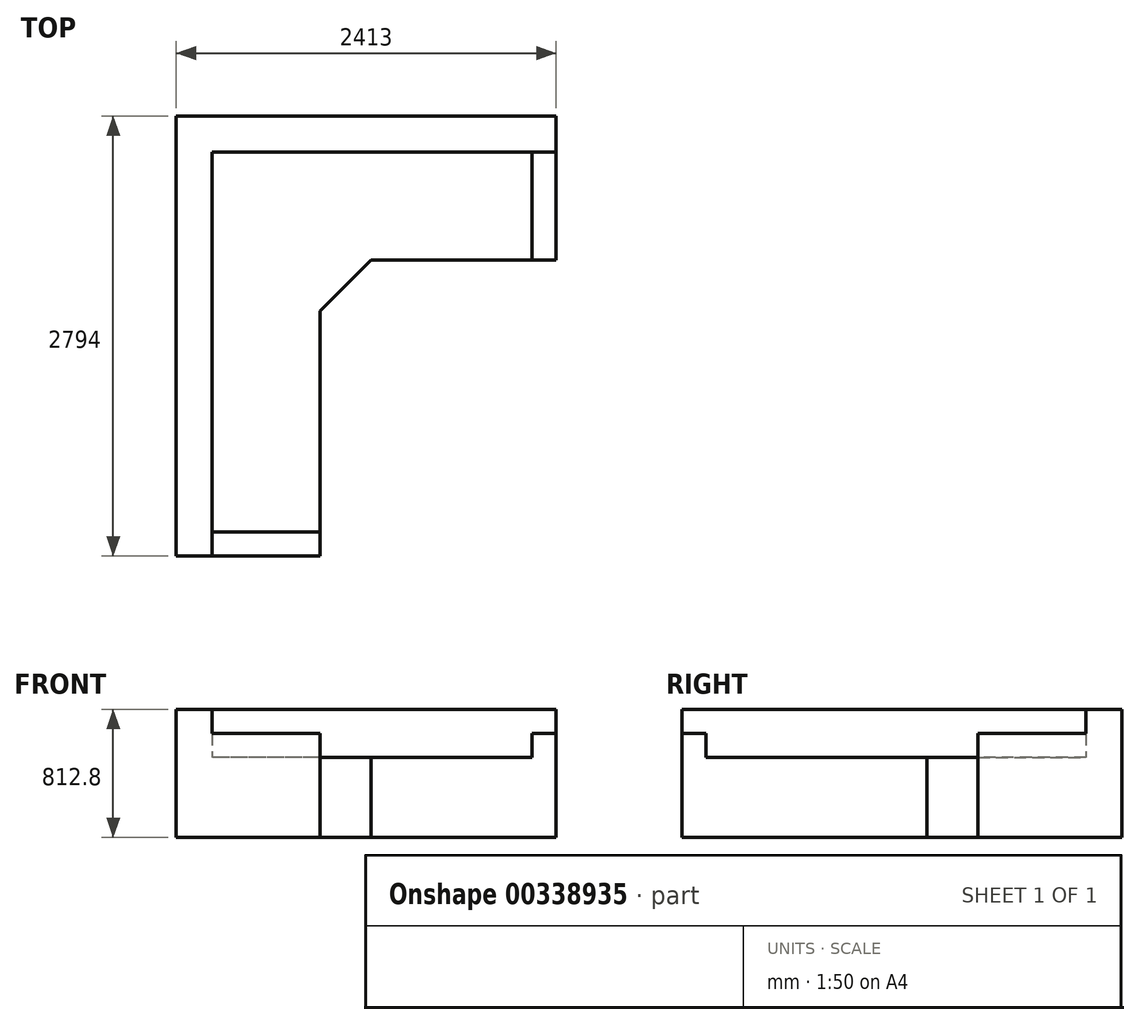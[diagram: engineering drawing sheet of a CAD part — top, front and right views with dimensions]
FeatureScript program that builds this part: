
annotation { "Feature Type Name" : "Feature", "Feature Type Description" : "" }
export const myFeature = defineFeature(function(context is Context, id is Id, definition is map)
    precondition{}
    {
        {
            var Q0;
            Q0=qCreatedBy(makeId("Top.planeOp"),FACE);
            var sketch = newSketch(context, id + "F0", { "sketchPlane" : qUnion([Q0])});
            skLineSegment(sketch, "E0", {"start": v(0, 0) * mm, "end": v(2413, 0) * mm});
            skLineSegment(sketch, "E1", {"start": v(0, 0) * mm, "end": v(0, -2794) * mm});
            skLineSegment(sketch, "E2", {"start": v(2413, 0) * mm, "end": v(2413, -914.4) * mm});
            skLineSegment(sketch, "E3", {"start": v(2413, -914.4) * mm, "end": v(1237.69, -914.4) * mm});
            skLineSegment(sketch, "E4", {"start": v(1237.69, -914.4) * mm, "end": v(914.4, -1237.69) * mm});
            skLineSegment(sketch, "E5", {"start": v(914.4, -1237.69) * mm, "end": v(914.4, -2794) * mm});
            skLineSegment(sketch, "E6", {"start": v(914.4, -2794) * mm, "end": v(0, -2794) * mm});
            skSolve(sketch);
        }
        {
            var Q0;
            Q0=makeQuery(id+"F0.imprint","IMPRINT",FACE,{"disambiguationData":[TD([[makeQuery(id+"F0.imprint","IMPRINT",EDGE,{"derivedFrom":sQuery(id+"F0.wireOp",EDGE,"E0")}),-1.0]])]});
            extrude(context, id + "F1", {"entities" : qUnion([Q0]), "depth" : 508 * mm});
        }
        {
            var Q0;
            Q0=makeQuery(id+"F1.opExtrude","CAP_FACE",FACE,{"disambiguationData":[OSD([sQuery(id+"F0.wireOp",EDGE,"E0"),sQuery(id+"F0.wireOp",EDGE,"E1"),sQuery(id+"F0.wireOp",EDGE,"E2"),sQuery(id+"F0.wireOp",EDGE,"E3"),sQuery(id+"F0.wireOp",EDGE,"E4"),sQuery(id+"F0.wireOp",EDGE,"E5"),sQuery(id+"F0.wireOp",EDGE,"E6")])],"isStart":false});
            var sketch = newSketch(context, id + "F2", { "sketchPlane" : qUnion([Q0])});
            skLineSegment(sketch, "E7", {"start": v(0, -2794) * mm, "end": v(0, 0) * mm});
            skLineSegment(sketch, "E8", {"start": v(0, 0) * mm, "end": v(2413, 0) * mm});
            skLineSegment(sketch, "E9", {"start": v(2413, 0) * mm, "end": v(2413, -228.6) * mm});
            skLineSegment(sketch, "E10", {"start": v(2413, -228.6) * mm, "end": v(228.6, -228.6) * mm});
            skLineSegment(sketch, "E11", {"start": v(228.6, -228.6) * mm, "end": v(228.6, -2794) * mm});
            skLineSegment(sketch, "E12", {"start": v(228.6, -2794) * mm, "end": v(0, -2794) * mm});
            skSolve(sketch);
        }
        {
            var Q0;
            Q0=makeQuery(id+"F2.imprint","IMPRINT",FACE,{"disambiguationData":[TD([[makeQuery(id+"F2.imprint","IMPRINT",EDGE,{"derivedFrom":sQuery(id+"F2.wireOp",EDGE,"E7")}),1.0]])]});
            extrude(context, id + "F3", {"entities" : qUnion([Q0]), "operationType" : NewBodyOperationType.ADD, "depth" : 304.8 * mm});
        }
        {
            var Q0;
            Q0=makeQuery(id+"F1.opExtrude","CAP_FACE",FACE,{"disambiguationData":[OSD([sQuery(id+"F0.wireOp",EDGE,"E0"),sQuery(id+"F0.wireOp",EDGE,"E1"),sQuery(id+"F0.wireOp",EDGE,"E2"),sQuery(id+"F0.wireOp",EDGE,"E3"),sQuery(id+"F0.wireOp",EDGE,"E4"),sQuery(id+"F0.wireOp",EDGE,"E5"),sQuery(id+"F0.wireOp",EDGE,"E6")])],"isStart":false});
            var sketch = newSketch(context, id + "F4", { "sketchPlane" : qUnion([Q0])});
            skLineSegment(sketch, "E13", {"start": v(2413, -228.6) * mm, "end": v(2413, -914.4) * mm});
            skLineSegment(sketch, "E14", {"start": v(2413, -914.4) * mm, "end": v(2260.6, -914.4) * mm});
            skLineSegment(sketch, "E15", {"start": v(2260.6, -914.4) * mm, "end": v(2260.6, -228.6) * mm});
            skLineSegment(sketch, "E16", {"start": v(2260.6, -228.6) * mm, "end": v(2413, -228.6) * mm});
            skLineSegment(sketch, "E17.bottom", {"start": v(914.4, -2794) * mm, "end": v(228.6, -2794) * mm});
            skLineSegment(sketch, "E17.top", {"start": v(914.4, -2641.6) * mm, "end": v(228.6, -2641.6) * mm});
            skLineSegment(sketch, "E17.left", {"start": v(914.4, -2794) * mm, "end": v(914.4, -2641.6) * mm});
            skLineSegment(sketch, "E17.right", {"start": v(228.6, -2794) * mm, "end": v(228.6, -2641.6) * mm});
            skSolve(sketch);
        }
        {
            var Q0;
            Q0=makeQuery(id+"F4.imprint","IMPRINT",FACE,{"disambiguationData":[TD([[makeQuery(id+"F4.imprint","IMPRINT",EDGE,{"derivedFrom":sQuery(id+"F4.wireOp",EDGE,"E13")}),-1.0]])]});
            var Q1;
            Q1=makeQuery(id+"F4.imprint","IMPRINT",FACE,{"disambiguationData":[TD([[makeQuery(id+"F4.imprint","IMPRINT",EDGE,{"derivedFrom":sQuery(id+"F4.wireOp",EDGE,"E17.bottom")}),-1.0]])]});
            extrude(context, id + "F5", {"entities" : qUnion([Q0, Q1]), "operationType" : NewBodyOperationType.ADD, "depth" : 152.4 * mm});
        }
    });
